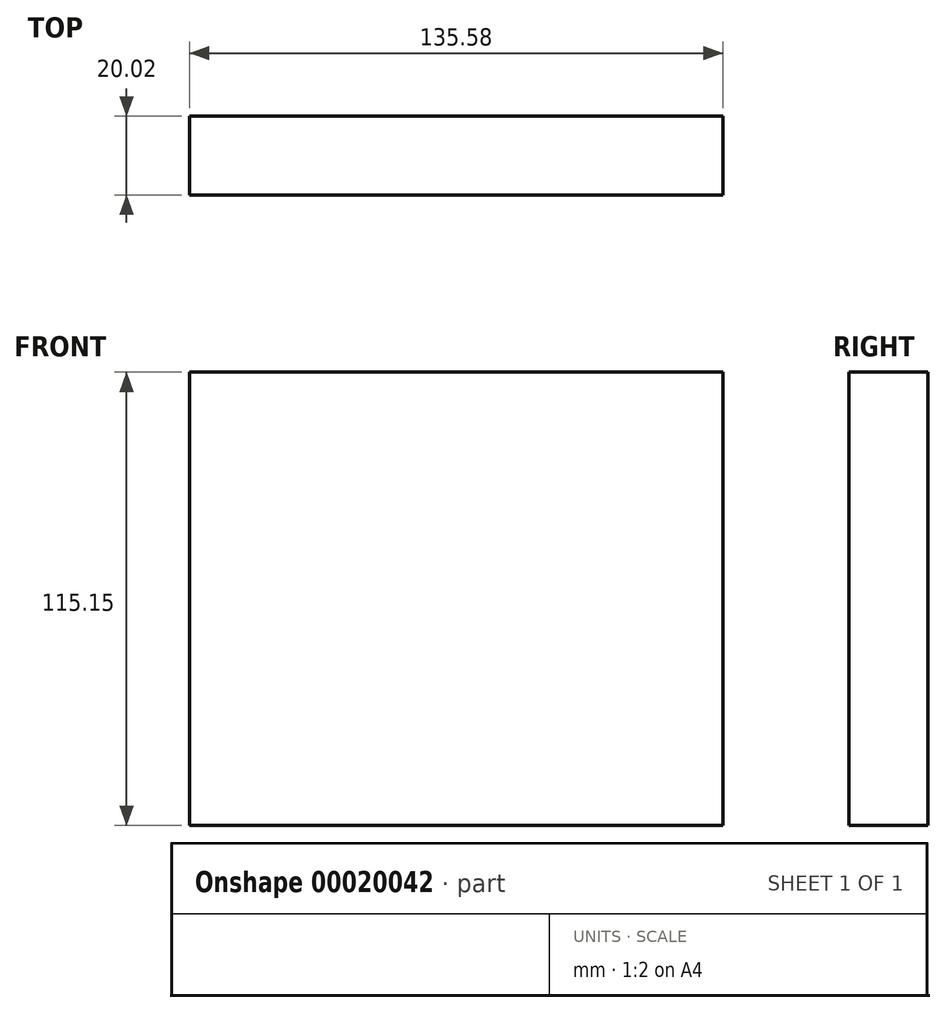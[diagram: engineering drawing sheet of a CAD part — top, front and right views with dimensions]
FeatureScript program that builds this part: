
annotation { "Feature Type Name" : "Feature", "Feature Type Description" : "" }
export const myFeature = defineFeature(function(context is Context, id is Id, definition is map)
    precondition{}
    {
        {
            var Q0;
            Q0=qCreatedBy(makeId("Front.planeOp"),FACE);
            var sketch = newSketch(context, id + "F0", { "sketchPlane" : qUnion([Q0])});
            skLineSegment(sketch, "E0.bottom", {"start": v(-70.65, 56.23) * mm, "end": v(64.93, 56.23) * mm});
            skLineSegment(sketch, "E0.top", {"start": v(-70.65, -58.92) * mm, "end": v(64.93, -58.92) * mm});
            skLineSegment(sketch, "E0.left", {"start": v(-70.65, 56.23) * mm, "end": v(-70.65, -58.92) * mm});
            skLineSegment(sketch, "E0.right", {"start": v(64.93, 56.23) * mm, "end": v(64.93, -58.92) * mm});
            skSolve(sketch);
        }
        {
            var Q0;
            Q0 = qSketchRegion(id + "F0", true);
            extrude(context, id + "F1", {"entities" : qUnion([Q0]), "depth" : 20.02 * mm});
        }
    });
